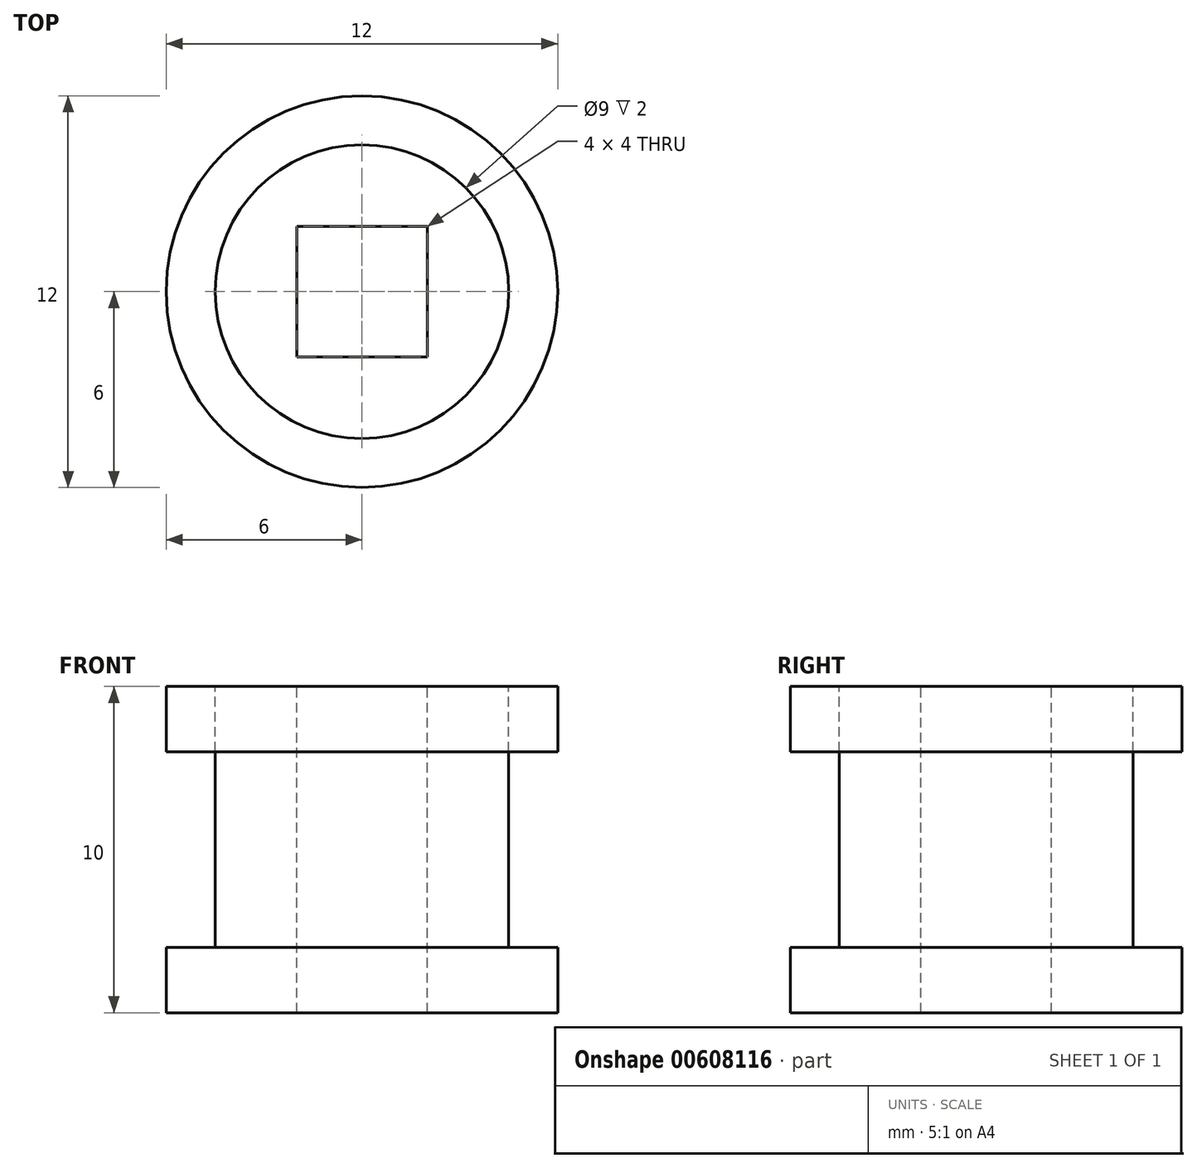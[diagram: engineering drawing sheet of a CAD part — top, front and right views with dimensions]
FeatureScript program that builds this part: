
annotation { "Feature Type Name" : "Feature", "Feature Type Description" : "" }
export const myFeature = defineFeature(function(context is Context, id is Id, definition is map)
    precondition{}
    {
        {
            var Q0;
            Q0=qCreatedBy(makeId("Top.planeOp"),FACE);
            var sketch = newSketch(context, id + "F0", { "sketchPlane" : qUnion([Q0])});
            skCircle(sketch, "E0", {"center": v(0, 0) * mm, "radius": 6 * mm});
            skCircle(sketch, "E1", {"center": v(0, 0) * mm, "radius": 4.5 * mm});
            skSolve(sketch);
        }
        {
            var Q0;
            Q0=makeQuery(id+"F0.imprint","IMPRINT",FACE,{"disambiguationData":[TD([[makeQuery(id+"F0.imprint","IMPRINT",EDGE,{"derivedFrom":sQuery(id+"F0.wireOp",EDGE,"E0")}),1.0]])]});
            extrude(context, id + "F1", {"entities" : qUnion([Q0]), "depth" : 2 * mm, "offsetDistance" : 25 * mm});
        }
        {
            var Q0;
            Q0=makeQuery(id+"F0.imprint","IMPRINT",FACE,{"disambiguationData":[TD([[makeQuery(id+"F0.imprint","IMPRINT",EDGE,{"derivedFrom":sQuery(id+"F0.wireOp",EDGE,"E1")}),1.0]])]});
            extrude(context, id + "F2", {"entities" : qUnion([Q0]), "operationType" : NewBodyOperationType.ADD, "depth" : 10 * mm, "offsetDistance" : 25 * mm});
        }
        {
            var Q0;
            Q0=makeQuery(id+"F2.opExtrude","CAP_FACE",FACE,{"disambiguationData":[OSD([sQuery(id+"F0.wireOp",EDGE,"E1")])],"isStart":false});
            var sketch = newSketch(context, id + "F3", { "sketchPlane" : qUnion([Q0])});
            skCircle(sketch, "E2", {"center": v(0, 0) * mm, "radius": 6 * mm});
            skLineSegment(sketch, "E3.bottom", {"start": v(2, -2) * mm, "end": v(-2, -2) * mm});
            skLineSegment(sketch, "E3.top", {"start": v(2, 2) * mm, "end": v(-2, 2) * mm});
            skLineSegment(sketch, "E3.left", {"start": v(2, -2) * mm, "end": v(2, 2) * mm});
            skLineSegment(sketch, "E3.right", {"start": v(-2, -2) * mm, "end": v(-2, 2) * mm});
            skSolve(sketch);
        }
        {
            var Q0;
            Q0=makeQuery(id+"F3.imprint","IMPRINT",FACE,{"disambiguationData":[TD([[makeQuery(id+"F3.imprint","IMPRINT",EDGE,{"derivedFrom":sQuery(id+"F3.wireOp",EDGE,"E2")}),1.0]])]});
            extrude(context, id + "F4", {"entities" : qUnion([Q0]), "oppositeDirection" : true, "depth" : 2 * mm, "offsetDistance" : 25 * mm});
        }
        {
            var Q0;
            Q0=makeQuery(id+"F3.imprint","IMPRINT",FACE,{"disambiguationData":[TD([[makeQuery(id+"F3.imprint","IMPRINT",EDGE,{"derivedFrom":sQuery(id+"F3.wireOp",EDGE,"E3.bottom")}),-1.0]])]});
            extrude(context, id + "F5", {"entities" : qUnion([Q0]), "operationType" : NewBodyOperationType.REMOVE, "oppositeDirection" : true, "depth" : 25 * mm, "offsetDistance" : 25 * mm});
        }
    });
